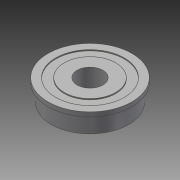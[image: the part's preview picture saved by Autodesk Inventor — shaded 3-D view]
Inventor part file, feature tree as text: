
AUTODESK INVENTOR PART (.ipt)
format: ipt  version: 2014 SP1 (Build 180222100, 222)  size: 120,320 bytes
history: native  units: in
note: dims shown in document units (in); Inventor stores cm internally (conversion verified against a paired STEP export)
features: revolve x1, imported_body x1
ambient origin geometry x8: Origin, YZ Plane, XZ Plane, XY Plane, X Axis, Y Axis, Z Axis, Center Point
bodies: Body1 (feature_tree)
feature tree (2):
  revolve  "Revolve1"  [1 undecoded]
  imported_body  "Base1"
note: 1 required parameter value undecoded (feature->parameter linkage not recoverable at this tier; creation-order binding heuristic only, values carry confidence <= 0.55)
